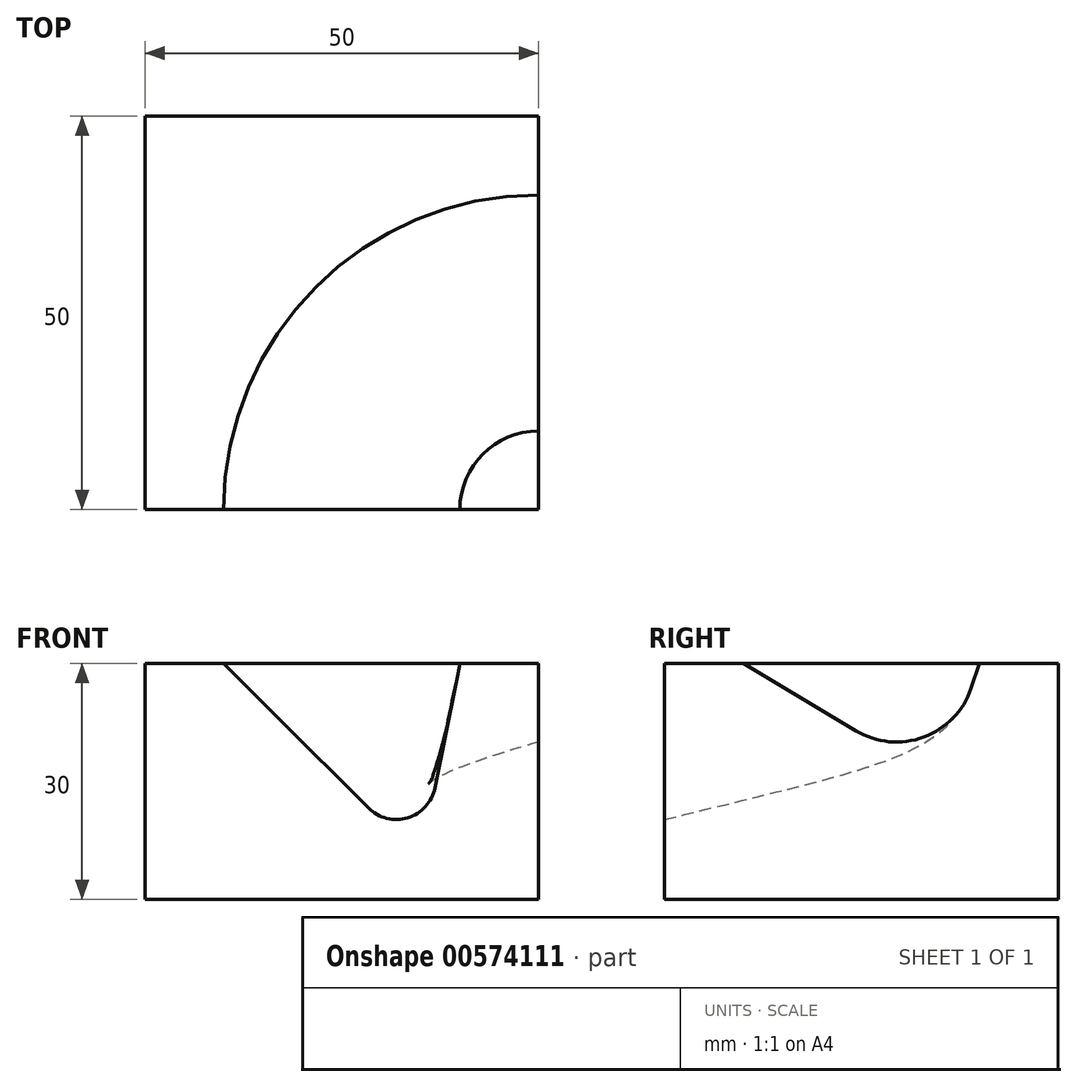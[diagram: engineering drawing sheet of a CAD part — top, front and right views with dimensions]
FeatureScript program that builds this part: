
annotation { "Feature Type Name" : "Feature", "Feature Type Description" : "" }
export const myFeature = defineFeature(function(context is Context, id is Id, definition is map)
    precondition{}
    {
        {
            var Q0;
            Q0=qCreatedBy(makeId("Top.planeOp"),FACE);
            var sketch = newSketch(context, id + "F0", { "sketchPlane" : qUnion([Q0])});
            skLineSegment(sketch, "E0.bottom", {"start": v(-25, 25) * mm, "end": v(25, 25) * mm});
            skLineSegment(sketch, "E0.top", {"start": v(-25, -25) * mm, "end": v(25, -25) * mm});
            skLineSegment(sketch, "E0.left", {"start": v(-25, 25) * mm, "end": v(-25, -25) * mm});
            skLineSegment(sketch, "E0.right", {"start": v(25, 25) * mm, "end": v(25, -25) * mm});
            skSolve(sketch);
        }
        {
            var Q0;
            Q0=makeQuery(id+"F0.imprint","IMPRINT",FACE,{"disambiguationData":[TD([[makeQuery(id+"F0.imprint","IMPRINT",EDGE,{"derivedFrom":sQuery(id+"F0.wireOp",EDGE,"E0.bottom")}),-1.0]])]});
            extrude(context, id + "F1", {"entities" : qUnion([Q0]), "depth" : 30 * mm, "offsetDistance" : 25 * mm});
        }
        {
            var Q0;
            Q0=makeQuery(id+"F1.opExtrude","CAP_FACE",FACE,{"disambiguationData":[OSD([sQuery(id+"F0.wireOp",EDGE,"E0.bottom"),sQuery(id+"F0.wireOp",EDGE,"E0.top"),sQuery(id+"F0.wireOp",EDGE,"E0.left"),sQuery(id+"F0.wireOp",EDGE,"E0.right")])],"isStart":false});
            var sketch = newSketch(context, id + "F2", { "sketchPlane" : qUnion([Q0])});
            skArc(sketch, "E1", {"start": v(15, -25) * mm, "mid": v(17.93, -17.93) * mm, "end": v(25, -15) * mm});
            skArc(sketch, "E2", {"start": v(-15, -25) * mm, "mid": v(-3.28, 3.28) * mm, "end": v(25, 15) * mm});
            skSolve(sketch);
        }
        {
            var Q0;
            Q0=makeQuery(id+"F1.opExtrude","SWEPT_FACE",FACE,{"disambiguationData":[OSD([sQuery(id+"F0.wireOp",EDGE,"E0.top")])]});
            var sketch = newSketch(context, id + "F3", { "sketchPlane" : qUnion([Q0])});
            skPoint(sketch, "E3.0", {"position": v(-15, 30) * mm});
            skPoint(sketch, "E4.0", {"position": v(15, 30) * mm});
            skLineSegment(sketch, "E5.0", {"start": v(-15, 30) * mm, "end": v(25, 30) * mm});
            skLineSegment(sketch, "E6", {"start": v(-15, 30) * mm, "end": v(3.4, 11.6) * mm});
            skLineSegment(sketch, "E7", {"start": v(11.83, 14.16) * mm, "end": v(15, 30) * mm});
            skLineSegment(sketch, "E8", {"start": v(15, 30) * mm, "end": v(15, 0) * mm, "construction": true});
            skPoint(sketch, "E9.visualSharp", {"position": v(10, 5) * mm});
            skArc(sketch, "E9.filletArc", {"start": v(3.4, 11.6) * mm, "mid": v(8.38, 10.36) * mm, "end": v(11.83, 14.16) * mm});
            skSolve(sketch);
        }
        {
            var Q0;
            Q0=makeQuery(id+"F1.opExtrude","SWEPT_FACE",FACE,{"disambiguationData":[OSD([sQuery(id+"F0.wireOp",EDGE,"E0.right")])]});
            var sketch = newSketch(context, id + "F4", { "sketchPlane" : qUnion([Q0])});
            skPoint(sketch, "E10.0", {"position": v(-15, 30) * mm});
            skPoint(sketch, "E11.0", {"position": v(15, 30) * mm});
            skLineSegment(sketch, "E12", {"start": v(-15, 30) * mm, "end": v(-0.69, 21.41) * mm});
            skLineSegment(sketch, "E13", {"start": v(13.94, 26.83) * mm, "end": v(15, 30) * mm});
            skPoint(sketch, "E14.visualSharp", {"position": v(10, 15) * mm});
            skArc(sketch, "E14.filletArc", {"start": v(-0.69, 21.41) * mm, "mid": v(7.92, 20.6) * mm, "end": v(13.94, 26.83) * mm});
            skSolve(sketch);
        }
        {
            var Q1;
            {var subQ0=sQuery(id+"F3.wireOp",EDGE,"E6");Q1=makeQuery(id+"F3.imprint","IMPRINT",FACE,{"disambiguationData":[TD([[makeQuery(id+"F3.imprint","IMPRINT",EDGE,{"derivedFrom":subQ0}),1.0]])]});}
            var Q2;
            {var subQ0=sQuery(id+"F4.wireOp",EDGE,"E12");Q2=makeQuery(id+"F4.imprint","IMPRINT",FACE,{"disambiguationData":[TD([[makeQuery(id+"F4.imprint","IMPRINT",EDGE,{"derivedFrom":subQ0}),1.0]])]});}
            var Q3;
            Q3=sQuery(id+"F2.wireOp",EDGE,"E1");
            var Q4;
            Q4=sQuery(id+"F2.wireOp",EDGE,"E2");
            loft(context, id + "F5", {"operationType" : NewBodyOperationType.REMOVE, "addGuides" : true, "sheetProfilesArray" : [{ "sheetProfileEntities" : qUnion([Q1]) }, { "sheetProfileEntities" : qUnion([Q2]) }], "guidesArray" : [{ "guideEntities" : qUnion([Q3]), "guideDerivativeType" : LoftGuideDerivativeType.DEFAULT, "guideDerivativeMagnitude" : 1 }, { "guideEntities" : qUnion([Q4]), "guideDerivativeType" : LoftGuideDerivativeType.DEFAULT, "guideDerivativeMagnitude" : 1 }]});
        }
    });
